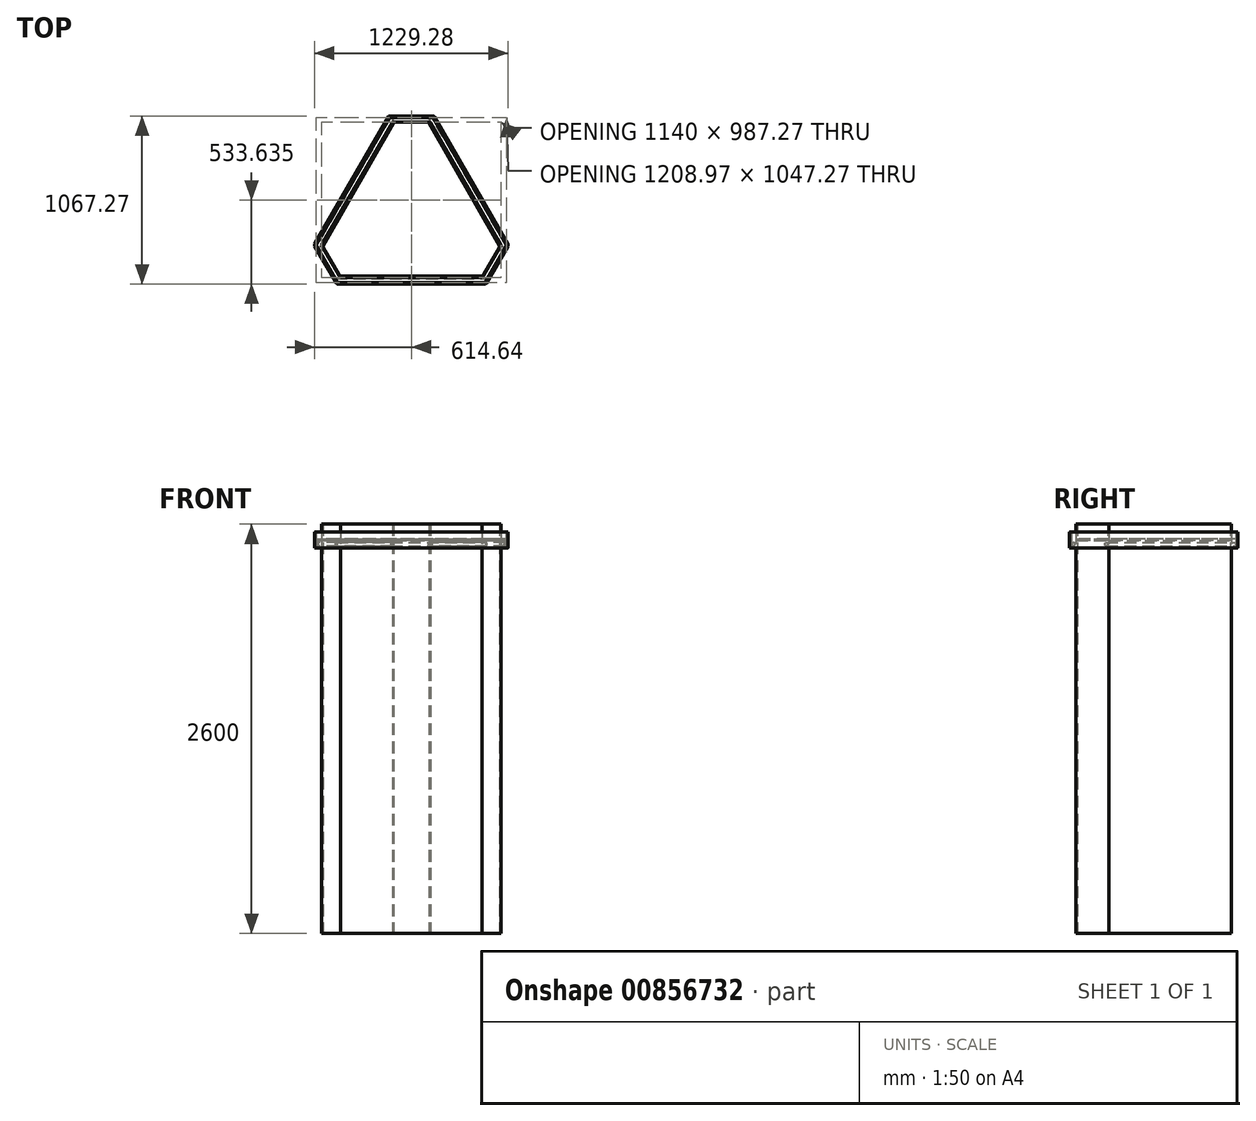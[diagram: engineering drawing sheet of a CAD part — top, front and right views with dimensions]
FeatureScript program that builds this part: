
annotation { "Feature Type Name" : "Feature", "Feature Type Description" : "" }
export const myFeature = defineFeature(function(context is Context, id is Id, definition is map)
    precondition{}
    {
        {
            var Q0;
            Q0=qCreatedBy(makeId("Top.planeOp"),FACE);
            var sketch = newSketch(context, id + "F0", { "sketchPlane" : qUnion([Q0])});
            skLineSegment(sketch, "E0", {"start": v(-570, 207.85) * mm, "end": v(-120, 987.27) * mm});
            skLineSegment(sketch, "E1", {"start": v(120, 987.27) * mm, "end": v(570, 207.85) * mm});
            skLineSegment(sketch, "E2", {"start": v(-450, 0) * mm, "end": v(450, 0) * mm});
            skLineSegment(sketch, "E3", {"start": v(-690, 0) * mm, "end": v(345, 597.56) * mm, "construction": true});
            skLineSegment(sketch, "E4", {"start": v(690, 0) * mm, "end": v(-345, 597.56) * mm, "construction": true});
            skLineSegment(sketch, "E5", {"start": v(0, 1195.12) * mm, "end": v(0, 0) * mm, "construction": true});
            skLineSegment(sketch, "E6", {"start": v(-120, 987.27) * mm, "end": v(120, 987.27) * mm});
            skLineSegment(sketch, "E7", {"start": v(-450, 0) * mm, "end": v(-570, 207.85) * mm});
            skLineSegment(sketch, "E8", {"start": v(450, 0) * mm, "end": v(570, 207.85) * mm});
            skSolve(sketch);
        }
        {
            var Q0;
            Q0=qSketchRegion(id+"F0",true);
            extrude(context, id + "F1", {"entities" : qUnion([Q0]), "depth" : 2600 * mm, "offsetDistance" : 25 * mm});
        }
        {
            var Q0;
            Q0=makeQuery(id+"F1.opExtrude","CAP_FACE",FACE,{"disambiguationData":[OSD([sQuery(id+"F0.wireOp",EDGE,"E0"),sQuery(id+"F0.wireOp",EDGE,"E1"),sQuery(id+"F0.wireOp",EDGE,"E2"),sQuery(id+"F0.wireOp",EDGE,"E6"),sQuery(id+"F0.wireOp",EDGE,"E7"),sQuery(id+"F0.wireOp",EDGE,"E8")])],"isStart":false});
            var sketch = newSketch(context, id + "F2", { "sketchPlane" : qUnion([Q0])});
            skLineSegment(sketch, "E9.0", {"start": v(-350, 40) * mm, "end": v(350, 40) * mm});
            skLineSegment(sketch, "E10.0", {"start": v(-485.36, 274.45) * mm, "end": v(-135.36, 880.67) * mm});
            skLineSegment(sketch, "E11", {"start": v(-350, 40) * mm, "end": v(-350, 90) * mm});
            skLineSegment(sketch, "E12", {"start": v(-350, 90) * mm, "end": v(350, 90) * mm});
            skLineSegment(sketch, "E13", {"start": v(350, 90) * mm, "end": v(350, 40) * mm});
            skLineSegment(sketch, "E14", {"start": v(-135.36, 880.67) * mm, "end": v(-92.06, 855.67) * mm});
            skLineSegment(sketch, "E15", {"start": v(-92.06, 855.67) * mm, "end": v(-442.06, 249.45) * mm});
            skLineSegment(sketch, "E16", {"start": v(-442.06, 249.45) * mm, "end": v(-485.36, 274.45) * mm});
            skLineSegment(sketch, "E17", {"start": v(-345, 597.56) * mm, "end": v(-140.02, 479.21) * mm, "construction": true});
            skLineSegment(sketch, "E18", {"start": v(0, 0) * mm, "end": v(0, 987.27) * mm, "construction": true});
            skLineSegment(sketch, "E19.MirrorCS", {"start": v(-92.06, 855.67) * mm, "end": v(-135.36, 880.67) * mm});
            skLineSegment(sketch, "E20.MirrorCS", {"start": v(-485.36, 274.45) * mm, "end": v(-442.06, 249.45) * mm});
            skLineSegment(sketch, "E21.MirrorCS", {"start": v(-135.36, 880.67) * mm, "end": v(-485.36, 274.45) * mm});
            skLineSegment(sketch, "E22.MirrorCS", {"start": v(-442.06, 249.45) * mm, "end": v(-92.06, 855.67) * mm});
            skLineSegment(sketch, "E23.MirrorCS", {"start": v(135.36, 880.67) * mm, "end": v(92.06, 855.67) * mm});
            skLineSegment(sketch, "E24.MirrorCS", {"start": v(442.06, 249.45) * mm, "end": v(485.36, 274.45) * mm});
            skLineSegment(sketch, "E25.MirrorCS", {"start": v(485.36, 274.45) * mm, "end": v(442.06, 249.45) * mm});
            skLineSegment(sketch, "E26.MirrorCS", {"start": v(92.06, 855.67) * mm, "end": v(135.36, 880.67) * mm});
            skLineSegment(sketch, "E27.MirrorCS", {"start": v(92.06, 855.67) * mm, "end": v(442.06, 249.45) * mm});
            skLineSegment(sketch, "E28.MirrorCS", {"start": v(485.36, 274.45) * mm, "end": v(135.36, 880.67) * mm});
            skLineSegment(sketch, "E29.MirrorCS", {"start": v(135.36, 880.67) * mm, "end": v(485.36, 274.45) * mm});
            skLineSegment(sketch, "E30.MirrorCS", {"start": v(442.06, 249.45) * mm, "end": v(92.06, 855.67) * mm});
            skSolve(sketch);
        }
        {
            var Q0;
            Q0=qCreatedBy(makeId("Right.planeOp"),FACE);
            var sketch = newSketch(context, id + "F3", { "sketchPlane" : qUnion([Q0])});
            skPoint(sketch, "E31.2", {"position": v(103.92, 2600) * mm});
            skLineSegment(sketch, "E32", {"start": v(398.37, 2400) * mm, "end": v(398.37, -119.7) * mm, "construction": true});
            skPoint(sketch, "E32.endSnap0", {"position": v(398.37, 2400) * mm});
            skSolve(sketch);
        }
        {
            var Q0;
            Q0=makeQuery(id+"F1.opExtrude","CAP_FACE",FACE,{"disambiguationData":[OSD([sQuery(id+"F0.wireOp",EDGE,"E0"),sQuery(id+"F0.wireOp",EDGE,"E1"),sQuery(id+"F0.wireOp",EDGE,"E2"),sQuery(id+"F0.wireOp",EDGE,"E6"),sQuery(id+"F0.wireOp",EDGE,"E7"),sQuery(id+"F0.wireOp",EDGE,"E8")])],"isStart":true});
            var sketch = newSketch(context, id + "F4", { "sketchPlane" : qUnion([Q0])});
            skLineSegment(sketch, "E33.0", {"start": v(-570, -207.85) * mm, "end": v(-120, -987.27) * mm});
            skLineSegment(sketch, "E33.1", {"start": v(120, -987.27) * mm, "end": v(570, -207.85) * mm});
            skLineSegment(sketch, "E33.2", {"start": v(-450, 0) * mm, "end": v(450, 0) * mm});
            skLineSegment(sketch, "E34.0", {"start": v(-561.34, -202.85) * mm, "end": v(-111.34, -982.27) * mm});
            skLineSegment(sketch, "E35.0", {"start": v(-450, -10) * mm, "end": v(450, -10) * mm});
            skLineSegment(sketch, "E36.0", {"start": v(111.34, -982.27) * mm, "end": v(561.34, -202.85) * mm});
            skLineSegment(sketch, "E37", {"start": v(-111.34, -982.27) * mm, "end": v(-120, -987.27) * mm});
            skLineSegment(sketch, "E38", {"start": v(-570, -207.85) * mm, "end": v(-561.34, -202.85) * mm});
            skLineSegment(sketch, "E39", {"start": v(-450, 0) * mm, "end": v(-450, -10) * mm});
            skLineSegment(sketch, "E40", {"start": v(450, 0) * mm, "end": v(450, -10) * mm});
            skLineSegment(sketch, "E41", {"start": v(570, -207.85) * mm, "end": v(561.34, -202.85) * mm});
            skLineSegment(sketch, "E42", {"start": v(120, -987.27) * mm, "end": v(111.34, -982.27) * mm});
            skSolve(sketch);
        }
        {
            var Q0;
            Q0=qSketchRegion(id+"F4",true);
            var Q1;
            Q1=makeQuery(id+"F1.opExtrude","CAP_FACE",FACE,{"disambiguationData":[OSD([sQuery(id+"F0.wireOp",EDGE,"E0"),sQuery(id+"F0.wireOp",EDGE,"E1"),sQuery(id+"F0.wireOp",EDGE,"E2"),sQuery(id+"F0.wireOp",EDGE,"E6"),sQuery(id+"F0.wireOp",EDGE,"E7"),sQuery(id+"F0.wireOp",EDGE,"E8")])],"isStart":false});
            extrude(context, id + "F5", {"entities" : qUnion([Q0]), "operationType" : NewBodyOperationType.REMOVE, "endBound" : BoundingType.UP_TO_SURFACE, "oppositeDirection" : true, "depth" : 25 * mm, "endBoundEntityFace" : qUnion([Q1]), "offsetDistance" : 25 * mm});
        }
        {
            var Q0;
            Q0=makeQuery(id+"F1.opExtrude","CAP_FACE",FACE,{"disambiguationData":[OSD([sQuery(id+"F0.wireOp",EDGE,"E0"),sQuery(id+"F0.wireOp",EDGE,"E1"),sQuery(id+"F0.wireOp",EDGE,"E2"),sQuery(id+"F0.wireOp",EDGE,"E6"),sQuery(id+"F0.wireOp",EDGE,"E7"),sQuery(id+"F0.wireOp",EDGE,"E8")])],"isStart":true});
            var sketch = newSketch(context, id + "F6", { "sketchPlane" : qUnion([Q0])});
            skLineSegment(sketch, "E43.0", {"start": v(-560.84, -203.71) * mm, "end": v(-111.84, -981.4) * mm});
            skLineSegment(sketch, "E44.0", {"start": v(-569.5, -208.71) * mm, "end": v(-120.5, -986.4) * mm});
            skLineSegment(sketch, "E45.0", {"start": v(-111.84, -981.4) * mm, "end": v(-120.5, -986.4) * mm});
            skLineSegment(sketch, "E46.0", {"start": v(-569.5, -208.71) * mm, "end": v(-560.84, -203.71) * mm});
            skPoint(sketch, "E47.orphan", {"position": v(-561.34, -202.85) * mm});
            skPoint(sketch, "E48.orphan", {"position": v(-111.34, -982.27) * mm});
            skSolve(sketch);
        }
        {
            var Q0;
            Q0=qSketchRegion(id+"F6",true);
            var Q1;
            Q1=makeQuery(id+"F1.opExtrude","CAP_FACE",FACE,{"disambiguationData":[OSD([sQuery(id+"F0.wireOp",EDGE,"E0"),sQuery(id+"F0.wireOp",EDGE,"E1"),sQuery(id+"F0.wireOp",EDGE,"E2"),sQuery(id+"F0.wireOp",EDGE,"E6"),sQuery(id+"F0.wireOp",EDGE,"E7"),sQuery(id+"F0.wireOp",EDGE,"E8")])],"isStart":false});
            extrude(context, id + "F7", {"entities" : qUnion([Q0]), "endBound" : BoundingType.UP_TO_SURFACE, "oppositeDirection" : true, "depth" : 25 * mm, "endBoundEntityFace" : qUnion([Q1]), "offsetDistance" : 25 * mm});
        }
        {
            var Q0;
            Q0=makeQuery(id+"F7.opExtrude","SWEPT_BODY",BODY,{"disambiguationData":[OSD([sQuery(id+"F6.wireOp",EDGE,"E43.0"),sQuery(id+"F6.wireOp",EDGE,"E44.0"),sQuery(id+"F6.wireOp",EDGE,"E45.0"),sQuery(id+"F6.wireOp",EDGE,"E46.0")])]});
            var Q1;
            Q1=sQuery(id+"F3.wireOp",EDGE,"E32");
            circularPattern(context, id + "F8", {"entities" : qUnion([Q0]), "axis" : qUnion([Q1]), "angle" : 360 * degree, "instanceCount" : 3, "equalSpace" : true});
        }
        {
            var Q0;
            Q0=makeQuery(id+"F1.opExtrude","SWEPT_FACE",FACE,{"disambiguationData":[OSD([sQuery(id+"F0.wireOp",EDGE,"E7")])]});
            var Q1;
            Q1=makeQuery(id+"F7.opExtrude","SWEPT_EDGE",EDGE,{"disambiguationData":[OSD([sQuery(id+"F6.wireOp",EDGE,"E44.0"),sQuery(id+"F6.wireOp",EDGE,"E46.0")])]});
            cPlane(context, id + "F9", {"entities" : qUnion([Q0, Q1]), "cplaneType" : CPlaneType.LINE_ANGLE, "offset" : 25 * mm, "angle" : 90 * degree, "width" : 150 * mm, "height" : 150 * mm});
        }
        {
            var Q0;
            Q0=qCreatedBy(id+"F9.planeOp",FACE);
            cPlane(context, id + "F10", {"entities" : qUnion([Q0]), "cplaneType" : CPlaneType.OFFSET, "offset" : 120.5 * mm, "width" : 150 * mm, "height" : 150 * mm});
        }
        {
            var Q0;
            Q0=makeQuery(id+"F1.opExtrude","CAP_FACE",FACE,{"disambiguationData":[OSD([sQuery(id+"F0.wireOp",EDGE,"E0"),sQuery(id+"F0.wireOp",EDGE,"E1"),sQuery(id+"F0.wireOp",EDGE,"E2"),sQuery(id+"F0.wireOp",EDGE,"E6"),sQuery(id+"F0.wireOp",EDGE,"E7"),sQuery(id+"F0.wireOp",EDGE,"E8")])],"isStart":false});
            cPlane(context, id + "F11", {"entities" : qUnion([Q0]), "cplaneType" : CPlaneType.OFFSET, "offset" : 100 * mm, "oppositeDirection" : true, "width" : 150 * mm, "height" : 150 * mm});
        }
        {
            var Q0;
            Q0=qCreatedBy(id+"F11.planeOp",FACE);
            var sketch = newSketch(context, id + "F12", { "sketchPlane" : qUnion([Q0])});
            skLineSegment(sketch, "E49.0", {"start": v(-450, 0) * mm, "end": v(-570, 207.85) * mm});
            skLineSegment(sketch, "E49.1", {"start": v(-120, 987.27) * mm, "end": v(120, 987.27) * mm});
            skLineSegment(sketch, "E49.2", {"start": v(450, 0) * mm, "end": v(570, 207.85) * mm});
            skLineSegment(sketch, "E50", {"start": v(-450, 0) * mm, "end": v(450, 0) * mm});
            skLineSegment(sketch, "E51", {"start": v(570, 207.85) * mm, "end": v(120, 987.27) * mm});
            skLineSegment(sketch, "E52", {"start": v(-120, 987.27) * mm, "end": v(-570, 207.85) * mm});
            skLineSegment(sketch, "E53.0", {"start": v(-473.1, -40) * mm, "end": v(473.1, -40) * mm});
            skLineSegment(sketch, "E53.1", {"start": v(-143.1, 1027.27) * mm, "end": v(-616.19, 207.85) * mm});
            skLineSegment(sketch, "E53.2", {"start": v(-143.1, 1027.27) * mm, "end": v(143.1, 1027.27) * mm});
            skLineSegment(sketch, "E53.3", {"start": v(-473.1, -40) * mm, "end": v(-616.19, 207.85) * mm});
            skLineSegment(sketch, "E53.4", {"start": v(616.19, 207.85) * mm, "end": v(143.1, 1027.27) * mm});
            skLineSegment(sketch, "E53.5", {"start": v(473.1, -40) * mm, "end": v(616.19, 207.85) * mm});
            skSolve(sketch);
        }
        {
            var Q0;
            Q0 = qSketchRegion(id + "F12", true);
            extrude(context, id + "F13", {"entities" : qUnion([Q0]), "depth" : 10 * mm, "offsetDistance" : 25 * mm, "symmetric" : true});
        }
        {
            var Q0;
            Q0=qCreatedBy(id+"F11.planeOp",FACE);
            var sketch = newSketch(context, id + "F14", { "sketchPlane" : qUnion([Q0])});
            skLineSegment(sketch, "E54.0", {"start": v(-473.1, -40) * mm, "end": v(473.1, -40) * mm});
            skLineSegment(sketch, "E54.1", {"start": v(-473.1, -40) * mm, "end": v(-616.19, 207.85) * mm});
            skLineSegment(sketch, "E54.2", {"start": v(-143.1, 1027.27) * mm, "end": v(-616.19, 207.85) * mm});
            skLineSegment(sketch, "E54.3", {"start": v(-143.1, 1027.27) * mm, "end": v(143.1, 1027.27) * mm});
            skLineSegment(sketch, "E54.4", {"start": v(616.19, 207.85) * mm, "end": v(143.1, 1027.27) * mm});
            skLineSegment(sketch, "E54.5", {"start": v(473.1, -40) * mm, "end": v(616.19, 207.85) * mm});
            skLineSegment(sketch, "E55.0", {"start": v(467.32, -30) * mm, "end": v(604.64, 207.85) * mm});
            skLineSegment(sketch, "E55.1", {"start": v(-137.32, 1017.27) * mm, "end": v(137.32, 1017.27) * mm});
            skLineSegment(sketch, "E55.2", {"start": v(-137.32, 1017.27) * mm, "end": v(-604.64, 207.85) * mm});
            skLineSegment(sketch, "E55.3", {"start": v(604.64, 207.85) * mm, "end": v(137.32, 1017.27) * mm});
            skLineSegment(sketch, "E55.4", {"start": v(-467.32, -30) * mm, "end": v(-604.64, 207.85) * mm});
            skLineSegment(sketch, "E55.5", {"start": v(-467.32, -30) * mm, "end": v(467.32, -30) * mm});
            skSolve(sketch);
        }
        {
            var Q0;
            Q0 = qSketchRegion(id + "F14", true);
            extrude(context, id + "F15", {"entities" : qUnion([Q0]), "operationType" : NewBodyOperationType.ADD, "depth" : 100 * mm, "offsetDistance" : 25 * mm, "symmetric" : true});
        }
        {
            var Q0;
            Q0=makeQuery(id+"F15.boolean.opBoolean","MERGE",EDGE,{"derivedFrom":[makeQuery(id+"F13.opExtrude","SWEPT_EDGE",EDGE,{"disambiguationData":[OSD([sQuery(id+"F12.wireOp",EDGE,"E53.1"),sQuery(id+"F12.wireOp",EDGE,"E53.3")])]}),makeQuery(id+"F15.opExtrude","SWEPT_EDGE",EDGE,{"disambiguationData":[OSD([sQuery(id+"F14.wireOp",EDGE,"E54.1"),sQuery(id+"F14.wireOp",EDGE,"E54.2")])]})]});
            var Q1;
            Q1=makeQuery(id+"F15.boolean.opBoolean","MERGE",EDGE,{"derivedFrom":[makeQuery(id+"F13.opExtrude","SWEPT_EDGE",EDGE,{"disambiguationData":[OSD([sQuery(id+"F12.wireOp",EDGE,"E53.0"),sQuery(id+"F12.wireOp",EDGE,"E53.3")])]}),makeQuery(id+"F15.opExtrude","SWEPT_EDGE",EDGE,{"disambiguationData":[OSD([sQuery(id+"F14.wireOp",EDGE,"E54.0"),sQuery(id+"F14.wireOp",EDGE,"E54.1")])]})]});
            var Q2;
            Q2=makeQuery(id+"F15.boolean.opBoolean","MERGE",EDGE,{"derivedFrom":[makeQuery(id+"F13.opExtrude","SWEPT_EDGE",EDGE,{"disambiguationData":[OSD([sQuery(id+"F12.wireOp",EDGE,"E53.0"),sQuery(id+"F12.wireOp",EDGE,"E53.5")])]}),makeQuery(id+"F15.opExtrude","SWEPT_EDGE",EDGE,{"disambiguationData":[OSD([sQuery(id+"F14.wireOp",EDGE,"E54.0"),sQuery(id+"F14.wireOp",EDGE,"E54.5")])]})]});
            var Q3;
            Q3=makeQuery(id+"F15.boolean.opBoolean","MERGE",EDGE,{"derivedFrom":[makeQuery(id+"F13.opExtrude","SWEPT_EDGE",EDGE,{"disambiguationData":[OSD([sQuery(id+"F12.wireOp",EDGE,"E53.4"),sQuery(id+"F12.wireOp",EDGE,"E53.5")])]}),makeQuery(id+"F15.opExtrude","SWEPT_EDGE",EDGE,{"disambiguationData":[OSD([sQuery(id+"F14.wireOp",EDGE,"E54.4"),sQuery(id+"F14.wireOp",EDGE,"E54.5")])]})]});
            var Q4;
            Q4=makeQuery(id+"F15.boolean.opBoolean","MERGE",EDGE,{"derivedFrom":[makeQuery(id+"F13.opExtrude","SWEPT_EDGE",EDGE,{"disambiguationData":[OSD([sQuery(id+"F12.wireOp",EDGE,"E53.2"),sQuery(id+"F12.wireOp",EDGE,"E53.4")])]}),makeQuery(id+"F15.opExtrude","SWEPT_EDGE",EDGE,{"disambiguationData":[OSD([sQuery(id+"F14.wireOp",EDGE,"E54.3"),sQuery(id+"F14.wireOp",EDGE,"E54.4")])]})]});
            var Q5;
            Q5=makeQuery(id+"F15.boolean.opBoolean","MERGE",EDGE,{"derivedFrom":[makeQuery(id+"F13.opExtrude","SWEPT_EDGE",EDGE,{"disambiguationData":[OSD([sQuery(id+"F12.wireOp",EDGE,"E53.1"),sQuery(id+"F12.wireOp",EDGE,"E53.2")])]}),makeQuery(id+"F15.opExtrude","SWEPT_EDGE",EDGE,{"disambiguationData":[OSD([sQuery(id+"F14.wireOp",EDGE,"E54.2"),sQuery(id+"F14.wireOp",EDGE,"E54.3")])]})]});
            fillet(context, id + "F16", {"entities" : qUnion([Q0, Q1, Q2, Q3, Q4, Q5]), "radius" : 10 * mm, "tangentPropagation" : true, "allowEdgeOverflow" : false});
        }
        {
            var Q0;
            {var subQ0=sQuery(id+"F14.wireOp",EDGE,"E55.3");var subQ1=sQuery(id+"F14.wireOp",EDGE,"E55.1");Q0=makeQuery(id+"F15.boolean.opBoolean","SPLIT",EDGE,{"disambiguationData":[TD([makeQuery(id+"F13.opExtrude","CAP_FACE",FACE,{"disambiguationData":[OSD([sQuery(id+"F12.wireOp",EDGE,"E49.0"),sQuery(id+"F12.wireOp",EDGE,"E49.1"),sQuery(id+"F12.wireOp",EDGE,"E49.2"),sQuery(id+"F12.wireOp",EDGE,"E50"),sQuery(id+"F12.wireOp",EDGE,"E51"),sQuery(id+"F12.wireOp",EDGE,"E52"),sQuery(id+"F12.wireOp",EDGE,"E53.0"),sQuery(id+"F12.wireOp",EDGE,"E53.1"),sQuery(id+"F12.wireOp",EDGE,"E53.2"),sQuery(id+"F12.wireOp",EDGE,"E53.3"),sQuery(id+"F12.wireOp",EDGE,"E53.4"),sQuery(id+"F12.wireOp",EDGE,"E53.5")])],"isStart":true})])],"derivedFrom":makeQuery(id+"F15.opExtrude","SWEPT_EDGE",EDGE,{"disambiguationData":[OSD([subQ1,subQ0])]})});}
            var Q1;
            {var subQ0=sQuery(id+"F14.wireOp",EDGE,"E55.2");var subQ1=sQuery(id+"F14.wireOp",EDGE,"E55.1");Q1=makeQuery(id+"F15.boolean.opBoolean","SPLIT",EDGE,{"disambiguationData":[TD([makeQuery(id+"F13.opExtrude","CAP_FACE",FACE,{"disambiguationData":[OSD([sQuery(id+"F12.wireOp",EDGE,"E49.0"),sQuery(id+"F12.wireOp",EDGE,"E49.1"),sQuery(id+"F12.wireOp",EDGE,"E49.2"),sQuery(id+"F12.wireOp",EDGE,"E50"),sQuery(id+"F12.wireOp",EDGE,"E51"),sQuery(id+"F12.wireOp",EDGE,"E52"),sQuery(id+"F12.wireOp",EDGE,"E53.0"),sQuery(id+"F12.wireOp",EDGE,"E53.1"),sQuery(id+"F12.wireOp",EDGE,"E53.2"),sQuery(id+"F12.wireOp",EDGE,"E53.3"),sQuery(id+"F12.wireOp",EDGE,"E53.4"),sQuery(id+"F12.wireOp",EDGE,"E53.5")])],"isStart":true})])],"derivedFrom":makeQuery(id+"F15.opExtrude","SWEPT_EDGE",EDGE,{"disambiguationData":[OSD([subQ1,subQ0])]})});}
            var Q2;
            {var subQ0=sQuery(id+"F14.wireOp",EDGE,"E55.0");var subQ1=sQuery(id+"F14.wireOp",EDGE,"E55.3");Q2=makeQuery(id+"F15.boolean.opBoolean","SPLIT",EDGE,{"disambiguationData":[TD([makeQuery(id+"F13.opExtrude","CAP_FACE",FACE,{"disambiguationData":[OSD([sQuery(id+"F12.wireOp",EDGE,"E49.0"),sQuery(id+"F12.wireOp",EDGE,"E49.1"),sQuery(id+"F12.wireOp",EDGE,"E49.2"),sQuery(id+"F12.wireOp",EDGE,"E50"),sQuery(id+"F12.wireOp",EDGE,"E51"),sQuery(id+"F12.wireOp",EDGE,"E52"),sQuery(id+"F12.wireOp",EDGE,"E53.0"),sQuery(id+"F12.wireOp",EDGE,"E53.1"),sQuery(id+"F12.wireOp",EDGE,"E53.2"),sQuery(id+"F12.wireOp",EDGE,"E53.3"),sQuery(id+"F12.wireOp",EDGE,"E53.4"),sQuery(id+"F12.wireOp",EDGE,"E53.5")])],"isStart":true})])],"derivedFrom":makeQuery(id+"F15.opExtrude","SWEPT_EDGE",EDGE,{"disambiguationData":[OSD([subQ0,subQ1])]})});}
            var Q3;
            {var subQ0=sQuery(id+"F14.wireOp",EDGE,"E55.0");var subQ1=sQuery(id+"F14.wireOp",EDGE,"E55.5");Q3=makeQuery(id+"F15.boolean.opBoolean","SPLIT",EDGE,{"disambiguationData":[TD([makeQuery(id+"F13.opExtrude","CAP_FACE",FACE,{"disambiguationData":[OSD([sQuery(id+"F12.wireOp",EDGE,"E49.0"),sQuery(id+"F12.wireOp",EDGE,"E49.1"),sQuery(id+"F12.wireOp",EDGE,"E49.2"),sQuery(id+"F12.wireOp",EDGE,"E50"),sQuery(id+"F12.wireOp",EDGE,"E51"),sQuery(id+"F12.wireOp",EDGE,"E52"),sQuery(id+"F12.wireOp",EDGE,"E53.0"),sQuery(id+"F12.wireOp",EDGE,"E53.1"),sQuery(id+"F12.wireOp",EDGE,"E53.2"),sQuery(id+"F12.wireOp",EDGE,"E53.3"),sQuery(id+"F12.wireOp",EDGE,"E53.4"),sQuery(id+"F12.wireOp",EDGE,"E53.5")])],"isStart":true})])],"derivedFrom":makeQuery(id+"F15.opExtrude","SWEPT_EDGE",EDGE,{"disambiguationData":[OSD([subQ0,subQ1])]})});}
            var Q4;
            {var subQ0=sQuery(id+"F14.wireOp",EDGE,"E55.4");var subQ1=sQuery(id+"F14.wireOp",EDGE,"E55.2");Q4=makeQuery(id+"F15.boolean.opBoolean","SPLIT",EDGE,{"disambiguationData":[TD([makeQuery(id+"F13.opExtrude","CAP_FACE",FACE,{"disambiguationData":[OSD([sQuery(id+"F12.wireOp",EDGE,"E49.0"),sQuery(id+"F12.wireOp",EDGE,"E49.1"),sQuery(id+"F12.wireOp",EDGE,"E49.2"),sQuery(id+"F12.wireOp",EDGE,"E50"),sQuery(id+"F12.wireOp",EDGE,"E51"),sQuery(id+"F12.wireOp",EDGE,"E52"),sQuery(id+"F12.wireOp",EDGE,"E53.0"),sQuery(id+"F12.wireOp",EDGE,"E53.1"),sQuery(id+"F12.wireOp",EDGE,"E53.2"),sQuery(id+"F12.wireOp",EDGE,"E53.3"),sQuery(id+"F12.wireOp",EDGE,"E53.4"),sQuery(id+"F12.wireOp",EDGE,"E53.5")])],"isStart":true})])],"derivedFrom":makeQuery(id+"F15.opExtrude","SWEPT_EDGE",EDGE,{"disambiguationData":[OSD([subQ1,subQ0])]})});}
            var Q5;
            {var subQ0=sQuery(id+"F14.wireOp",EDGE,"E55.5");var subQ1=sQuery(id+"F14.wireOp",EDGE,"E55.4");Q5=makeQuery(id+"F15.boolean.opBoolean","SPLIT",EDGE,{"disambiguationData":[TD([makeQuery(id+"F13.opExtrude","CAP_FACE",FACE,{"disambiguationData":[OSD([sQuery(id+"F12.wireOp",EDGE,"E49.0"),sQuery(id+"F12.wireOp",EDGE,"E49.1"),sQuery(id+"F12.wireOp",EDGE,"E49.2"),sQuery(id+"F12.wireOp",EDGE,"E50"),sQuery(id+"F12.wireOp",EDGE,"E51"),sQuery(id+"F12.wireOp",EDGE,"E52"),sQuery(id+"F12.wireOp",EDGE,"E53.0"),sQuery(id+"F12.wireOp",EDGE,"E53.1"),sQuery(id+"F12.wireOp",EDGE,"E53.2"),sQuery(id+"F12.wireOp",EDGE,"E53.3"),sQuery(id+"F12.wireOp",EDGE,"E53.4"),sQuery(id+"F12.wireOp",EDGE,"E53.5")])],"isStart":true})])],"derivedFrom":makeQuery(id+"F15.opExtrude","SWEPT_EDGE",EDGE,{"disambiguationData":[OSD([subQ1,subQ0])]})});}
            var Q6;
            {var subQ0=sQuery(id+"F14.wireOp",EDGE,"E55.5");var subQ1=sQuery(id+"F14.wireOp",EDGE,"E55.0");Q6=makeQuery(id+"F15.boolean.opBoolean","SPLIT",EDGE,{"disambiguationData":[TD([makeQuery(id+"F13.opExtrude","CAP_FACE",FACE,{"disambiguationData":[OSD([sQuery(id+"F12.wireOp",EDGE,"E49.0"),sQuery(id+"F12.wireOp",EDGE,"E49.1"),sQuery(id+"F12.wireOp",EDGE,"E49.2"),sQuery(id+"F12.wireOp",EDGE,"E50"),sQuery(id+"F12.wireOp",EDGE,"E51"),sQuery(id+"F12.wireOp",EDGE,"E52"),sQuery(id+"F12.wireOp",EDGE,"E53.0"),sQuery(id+"F12.wireOp",EDGE,"E53.1"),sQuery(id+"F12.wireOp",EDGE,"E53.2"),sQuery(id+"F12.wireOp",EDGE,"E53.3"),sQuery(id+"F12.wireOp",EDGE,"E53.4"),sQuery(id+"F12.wireOp",EDGE,"E53.5")])],"isStart":false})])],"derivedFrom":makeQuery(id+"F15.opExtrude","SWEPT_EDGE",EDGE,{"disambiguationData":[OSD([subQ1,subQ0])]})});}
            var Q7;
            {var subQ0=sQuery(id+"F14.wireOp",EDGE,"E55.3");var subQ1=sQuery(id+"F14.wireOp",EDGE,"E55.0");Q7=makeQuery(id+"F15.boolean.opBoolean","SPLIT",EDGE,{"disambiguationData":[TD([makeQuery(id+"F13.opExtrude","CAP_FACE",FACE,{"disambiguationData":[OSD([sQuery(id+"F12.wireOp",EDGE,"E49.0"),sQuery(id+"F12.wireOp",EDGE,"E49.1"),sQuery(id+"F12.wireOp",EDGE,"E49.2"),sQuery(id+"F12.wireOp",EDGE,"E50"),sQuery(id+"F12.wireOp",EDGE,"E51"),sQuery(id+"F12.wireOp",EDGE,"E52"),sQuery(id+"F12.wireOp",EDGE,"E53.0"),sQuery(id+"F12.wireOp",EDGE,"E53.1"),sQuery(id+"F12.wireOp",EDGE,"E53.2"),sQuery(id+"F12.wireOp",EDGE,"E53.3"),sQuery(id+"F12.wireOp",EDGE,"E53.4"),sQuery(id+"F12.wireOp",EDGE,"E53.5")])],"isStart":false})])],"derivedFrom":makeQuery(id+"F15.opExtrude","SWEPT_EDGE",EDGE,{"disambiguationData":[OSD([subQ1,subQ0])]})});}
            var Q8;
            {var subQ0=sQuery(id+"F14.wireOp",EDGE,"E55.1");var subQ1=sQuery(id+"F14.wireOp",EDGE,"E55.3");Q8=makeQuery(id+"F15.boolean.opBoolean","SPLIT",EDGE,{"disambiguationData":[TD([makeQuery(id+"F13.opExtrude","CAP_FACE",FACE,{"disambiguationData":[OSD([sQuery(id+"F12.wireOp",EDGE,"E49.0"),sQuery(id+"F12.wireOp",EDGE,"E49.1"),sQuery(id+"F12.wireOp",EDGE,"E49.2"),sQuery(id+"F12.wireOp",EDGE,"E50"),sQuery(id+"F12.wireOp",EDGE,"E51"),sQuery(id+"F12.wireOp",EDGE,"E52"),sQuery(id+"F12.wireOp",EDGE,"E53.0"),sQuery(id+"F12.wireOp",EDGE,"E53.1"),sQuery(id+"F12.wireOp",EDGE,"E53.2"),sQuery(id+"F12.wireOp",EDGE,"E53.3"),sQuery(id+"F12.wireOp",EDGE,"E53.4"),sQuery(id+"F12.wireOp",EDGE,"E53.5")])],"isStart":false})])],"derivedFrom":makeQuery(id+"F15.opExtrude","SWEPT_EDGE",EDGE,{"disambiguationData":[OSD([subQ0,subQ1])]})});}
            var Q9;
            {var subQ0=sQuery(id+"F14.wireOp",EDGE,"E55.1");var subQ1=sQuery(id+"F14.wireOp",EDGE,"E55.2");Q9=makeQuery(id+"F15.boolean.opBoolean","SPLIT",EDGE,{"disambiguationData":[TD([makeQuery(id+"F13.opExtrude","CAP_FACE",FACE,{"disambiguationData":[OSD([sQuery(id+"F12.wireOp",EDGE,"E49.0"),sQuery(id+"F12.wireOp",EDGE,"E49.1"),sQuery(id+"F12.wireOp",EDGE,"E49.2"),sQuery(id+"F12.wireOp",EDGE,"E50"),sQuery(id+"F12.wireOp",EDGE,"E51"),sQuery(id+"F12.wireOp",EDGE,"E52"),sQuery(id+"F12.wireOp",EDGE,"E53.0"),sQuery(id+"F12.wireOp",EDGE,"E53.1"),sQuery(id+"F12.wireOp",EDGE,"E53.2"),sQuery(id+"F12.wireOp",EDGE,"E53.3"),sQuery(id+"F12.wireOp",EDGE,"E53.4"),sQuery(id+"F12.wireOp",EDGE,"E53.5")])],"isStart":false})])],"derivedFrom":makeQuery(id+"F15.opExtrude","SWEPT_EDGE",EDGE,{"disambiguationData":[OSD([subQ0,subQ1])]})});}
            var Q10;
            {var subQ0=sQuery(id+"F14.wireOp",EDGE,"E55.4");var subQ1=sQuery(id+"F14.wireOp",EDGE,"E55.2");Q10=makeQuery(id+"F15.boolean.opBoolean","SPLIT",EDGE,{"disambiguationData":[TD([makeQuery(id+"F13.opExtrude","CAP_FACE",FACE,{"disambiguationData":[OSD([sQuery(id+"F12.wireOp",EDGE,"E49.0"),sQuery(id+"F12.wireOp",EDGE,"E49.1"),sQuery(id+"F12.wireOp",EDGE,"E49.2"),sQuery(id+"F12.wireOp",EDGE,"E50"),sQuery(id+"F12.wireOp",EDGE,"E51"),sQuery(id+"F12.wireOp",EDGE,"E52"),sQuery(id+"F12.wireOp",EDGE,"E53.0"),sQuery(id+"F12.wireOp",EDGE,"E53.1"),sQuery(id+"F12.wireOp",EDGE,"E53.2"),sQuery(id+"F12.wireOp",EDGE,"E53.3"),sQuery(id+"F12.wireOp",EDGE,"E53.4"),sQuery(id+"F12.wireOp",EDGE,"E53.5")])],"isStart":false})])],"derivedFrom":makeQuery(id+"F15.opExtrude","SWEPT_EDGE",EDGE,{"disambiguationData":[OSD([subQ1,subQ0])]})});}
            var Q11;
            {var subQ0=sQuery(id+"F14.wireOp",EDGE,"E55.5");var subQ1=sQuery(id+"F14.wireOp",EDGE,"E55.4");Q11=makeQuery(id+"F15.boolean.opBoolean","SPLIT",EDGE,{"disambiguationData":[TD([makeQuery(id+"F13.opExtrude","CAP_FACE",FACE,{"disambiguationData":[OSD([sQuery(id+"F12.wireOp",EDGE,"E49.0"),sQuery(id+"F12.wireOp",EDGE,"E49.1"),sQuery(id+"F12.wireOp",EDGE,"E49.2"),sQuery(id+"F12.wireOp",EDGE,"E50"),sQuery(id+"F12.wireOp",EDGE,"E51"),sQuery(id+"F12.wireOp",EDGE,"E52"),sQuery(id+"F12.wireOp",EDGE,"E53.0"),sQuery(id+"F12.wireOp",EDGE,"E53.1"),sQuery(id+"F12.wireOp",EDGE,"E53.2"),sQuery(id+"F12.wireOp",EDGE,"E53.3"),sQuery(id+"F12.wireOp",EDGE,"E53.4"),sQuery(id+"F12.wireOp",EDGE,"E53.5")])],"isStart":false})])],"derivedFrom":makeQuery(id+"F15.opExtrude","SWEPT_EDGE",EDGE,{"disambiguationData":[OSD([subQ1,subQ0])]})});}
            fillet(context, id + "F17", {"entities" : qUnion([Q0, Q1, Q2, Q3, Q4, Q5, Q6, Q7, Q8, Q9, Q10, Q11]), "radius" : 1 * mm, "tangentPropagation" : true, "allowEdgeOverflow" : false});
        }
        {
            var Q0;
            Q0=qCreatedBy(id+"F10.planeOp",FACE);
            var sketch = newSketch(context, id + "F18", { "sketchPlane" : qUnion([Q0])});
            skLineSegment(sketch, "E56.0", {"start": v(627.06, 2495) * mm, "end": v(627.06, 2450) * mm, "construction": true});
            skLineSegment(sketch, "E57.1", {"start": v(597.56, 2600) * mm, "end": v(597.56, 0) * mm, "construction": true});
            skLineSegment(sketch, "E58.0", {"start": v(627.06, 2495) * mm, "end": v(390.21, 2495) * mm, "construction": true});
            skCircle(sketch, "E59", {"center": v(612.3, 2472.5) * mm, "radius": 10 * mm});
            skPoint(sketch, "E59.centerSnap0", {"position": v(627.06, 2472.5) * mm});
            skSolve(sketch);
        }
        {
            var Q0;
            Q0 = qSketchRegion(id + "F18", true);
            var Q1;
            {var subQ2=sQuery(id+"F14.wireOp",EDGE,"E55.0");Q1=makeQuery(id+"F15.boolean.opBoolean","SPLIT",FACE,{"disambiguationData":[TD([makeQuery(id+"F13.opExtrude","CAP_FACE",FACE,{"disambiguationData":[OSD([sQuery(id+"F12.wireOp",EDGE,"E49.0"),sQuery(id+"F12.wireOp",EDGE,"E49.1"),sQuery(id+"F12.wireOp",EDGE,"E49.2"),sQuery(id+"F12.wireOp",EDGE,"E50"),sQuery(id+"F12.wireOp",EDGE,"E51"),sQuery(id+"F12.wireOp",EDGE,"E52"),sQuery(id+"F12.wireOp",EDGE,"E53.0"),sQuery(id+"F12.wireOp",EDGE,"E53.1"),sQuery(id+"F12.wireOp",EDGE,"E53.2"),sQuery(id+"F12.wireOp",EDGE,"E53.3"),sQuery(id+"F12.wireOp",EDGE,"E53.4"),sQuery(id+"F12.wireOp",EDGE,"E53.5")])],"isStart":true})])],"derivedFrom":makeQuery(id+"F15.opExtrude","SWEPT_FACE",FACE,{"disambiguationData":[OSD([subQ2])]})});}
            var Q2;
            {var subQ2=sQuery(id+"F14.wireOp",EDGE,"E55.1");Q2=makeQuery(id+"F15.boolean.opBoolean","SPLIT",FACE,{"disambiguationData":[TD([makeQuery(id+"F13.opExtrude","CAP_FACE",FACE,{"disambiguationData":[OSD([sQuery(id+"F12.wireOp",EDGE,"E49.0"),sQuery(id+"F12.wireOp",EDGE,"E49.1"),sQuery(id+"F12.wireOp",EDGE,"E49.2"),sQuery(id+"F12.wireOp",EDGE,"E50"),sQuery(id+"F12.wireOp",EDGE,"E51"),sQuery(id+"F12.wireOp",EDGE,"E52"),sQuery(id+"F12.wireOp",EDGE,"E53.0"),sQuery(id+"F12.wireOp",EDGE,"E53.1"),sQuery(id+"F12.wireOp",EDGE,"E53.2"),sQuery(id+"F12.wireOp",EDGE,"E53.3"),sQuery(id+"F12.wireOp",EDGE,"E53.4"),sQuery(id+"F12.wireOp",EDGE,"E53.5")])],"isStart":true})])],"derivedFrom":makeQuery(id+"F15.opExtrude","SWEPT_FACE",FACE,{"disambiguationData":[OSD([subQ2])]})});}
            extrude(context, id + "F19", {"entities" : qUnion([Q0]), "endBound" : BoundingType.UP_TO_SURFACE, "depth" : 25 * mm, "endBoundEntityFace" : qUnion([Q1]), "offsetDistance" : 25 * mm, "hasSecondDirection" : true, "secondDirectionBound" : BoundingType.UP_TO_SURFACE, "secondDirectionOppositeDirection" : true, "secondDirectionDepth" : 25 * mm, "secondDirectionBoundEntityFace" : qUnion([Q2])});
        }
        {
            var Q0;
            Q0=makeQuery(id+"F19.opExtrude","SWEPT_BODY",BODY,{"disambiguationData":[OSD([sQuery(id+"F18.wireOp",EDGE,"E59")])]});
            var Q1;
            Q1=sQuery(id+"F3.wireOp",EDGE,"E32");
            circularPattern(context, id + "F20", {"entities" : qUnion([Q0]), "axis" : qUnion([Q1]), "angle" : 360 * degree, "instanceCount" : 3, "equalSpace" : true});
        }
    });
